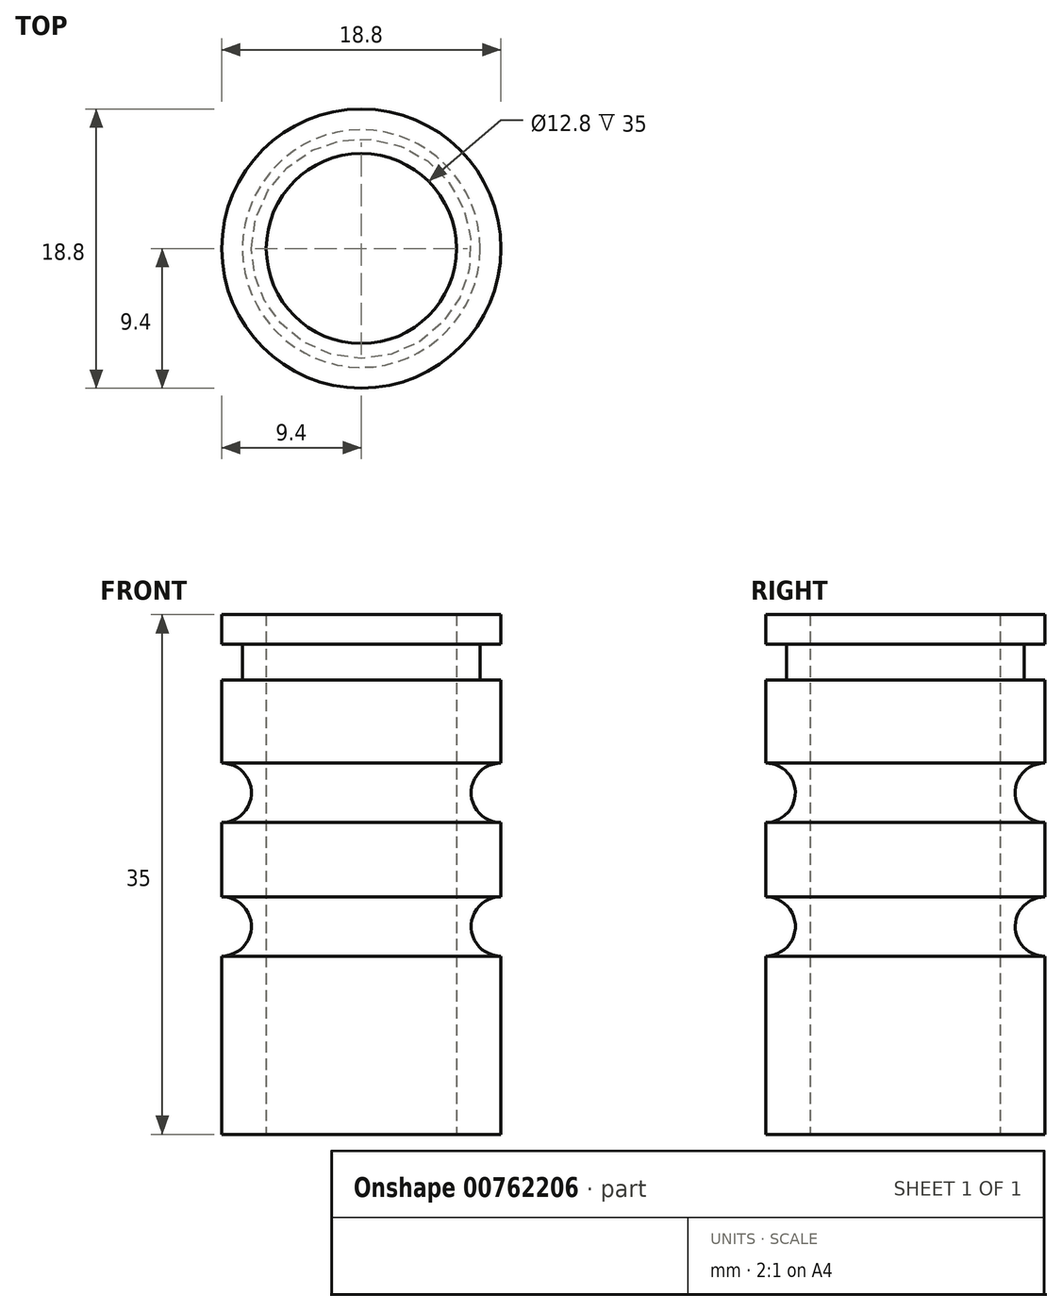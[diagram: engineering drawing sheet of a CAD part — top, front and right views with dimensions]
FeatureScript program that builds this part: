
annotation { "Feature Type Name" : "Feature", "Feature Type Description" : "" }
export const myFeature = defineFeature(function(context is Context, id is Id, definition is map)
    precondition{}
    {
        {
            var Q0;
            Q0=qCreatedBy(makeId("Right.planeOp"),FACE);
            var sketch = newSketch(context, id + "F0", { "sketchPlane" : qUnion([Q0])});
            skLineSegment(sketch, "E0", {"start": v(-6.4, 15) * mm, "end": v(-9.4, 15) * mm});
            skLineSegment(sketch, "E1", {"start": v(-6.4, 15) * mm, "end": v(-6.4, -20) * mm});
            skLineSegment(sketch, "E2", {"start": v(-6.4, -20) * mm, "end": v(-9.4, -20) * mm});
            skLineSegment(sketch, "E3", {"start": v(-9.4, 1) * mm, "end": v(-9.4, -4) * mm});
            skLineSegment(sketch, "E4", {"start": v(-9.4, -8) * mm, "end": v(-9.4, -20) * mm});
            skArc(sketch, "E5", {"start": v(-9.4, 1) * mm, "mid": v(-7.4, 3) * mm, "end": v(-9.4, 5) * mm});
            skArc(sketch, "E6", {"start": v(-9.4, -8) * mm, "mid": v(-7.4, -6) * mm, "end": v(-9.4, -4) * mm});
            skLineSegment(sketch, "E7", {"start": v(-9.4, 15) * mm, "end": v(-9.4, 13) * mm});
            skLineSegment(sketch, "E8", {"start": v(-9.4, 13) * mm, "end": v(-8, 13) * mm});
            skLineSegment(sketch, "E9", {"start": v(-8, 13) * mm, "end": v(-8, 10.6) * mm});
            skLineSegment(sketch, "E10", {"start": v(-8, 10.6) * mm, "end": v(-9.4, 10.6) * mm});
            skLineSegment(sketch, "E11", {"start": v(-9.4, 10.6) * mm, "end": v(-9.4, 5) * mm});
            skLineSegment(sketch, "E12", {"start": v(0, -22.58) * mm, "end": v(0, 18.96) * mm, "construction": true});
            skSolve(sketch);
        }
        {
            var Q0;
            Q0=makeQuery(id+"F0.imprint","IMPRINT",FACE,{"disambiguationData":[TD([[makeQuery(id+"F0.imprint","IMPRINT",EDGE,{"derivedFrom":sQuery(id+"F0.wireOp",EDGE,"E0")}),1.0]])]});
            var Q1;
            Q1=sQuery(id+"F0.wireOp",EDGE,"E12");
            revolve(context, id + "F1", {"surfaceOperationType" : NewSurfaceOperationType.NEW, "entities" : qUnion([Q0]), "axis" : qUnion([Q1]), "revolveType" : RevolveType.FULL});
        }
    });
